# Revit family: VRF_MMYS6HT8P_08-12_Outdoor Unit
name_source: partatom
category: Mechanical Equipment
revit_build: Autodesk Revit 2017 (Build: 20160225_1515(x64)
units: mm (PartAtom-declared; Revit-internal decimal feet)

## family parameters
Always vertical = Yes
Cut with Voids When Loaded = No
OmniClass Number = 23.75.00.00
OmniClass Title = Climate Control (HVAC)
Part Type = Normal
Room Calculation Point = No
Round Connector Dimension = Use Diameter
Shared = No
Work Plane-Based = No

## types (3) — shared parameters
Article Description = SMMSe stand alone
Capacity = -
Compressor detail - Type = Hermetic twin rotary compressor
Content Supplier URL = www.hcltech.com
Depth (mm) = 790 mm  [stored 2.59186 ft]
Description = SMMSe stand alone
Duct diameters(mm) = -
EMCS = 4
ETIM Article Class = EC001213
Energy class = -
Frequency (Hz) = 3Phase , 50Hz
Height (mm) = 1830 mm  [stored 6.00394 ft]
MEPcontent Class = HEATPUMP
Manufacturer = Toshiba
Manufacturer URL = https://www.toshiba-carrier.co.jp
Operating range - Cooling (°C) = -10  -  46
Operating range - Heating (°C) = -25  -  15.5
Part load = 30-100%
Piping diameter(mm)-Gas = 19.1
Piping diameter(mm)-Liquid = 12.7
Product Line = TCTC
Rated efficiency = -
Red = Colour RGB-255 000 000
Refrigerrant Type = R410A
Revit Version = 2017
Starting current = Soft Start
Static pressure = -
URL = https://www.toshiba-carrier.co.jp
Water pipe = -
Weight (Kg) = 227
White = Colour RGB-255 255 255
Width (mm) = 990 mm  [stored 3.24803 ft]

## per-type parameters (varying)
| type | Airflow (m3/h) | Capacities-Cooling (kW) | Capacities-Heating (kW) | Compressor detail - Motor output ( kW) | MCA (A) | MOCP (A) | Power consumption - Cooling | Power consumption - Heating | Rated efficiency - EER / COP | Running current - Cooling | Running current - Heating | Sound pressure - Cooling (dB)(A) | Sound pressure - Heating (dB)(A) | Voltage (V) |
| MMY-SAP0806HT8P-E | 9700 | 22.4 | 25.0 | 2.1 x 2 | 20.5 | 25.0 | 5.54 | 5.65 | 4.04 / 4.42 | 8.79 | 8.96 | 55.0 | 56.0 | 380 - 415V |
| MMY-SAP1006HT8P-E | 9700 | 28.0 | 31.5 | 3.1 x 2 | 21.5 | 25.0 | 7.9 | 7.59 | 3.54 / 4.15 | 12.4 | 11.9 | 57.0 | 58.0 | 380 - 415V |
| MMY-SAP1206HT8P-E | 12,200 | 33.5 | 37.5 | 3.9 x 2 | 26.1 | 32.0 | 10.3 | 9.76 | 3.25 / 3.84 | 16 | 15.1 | 59 | 61 | 380-415V |

note: column(s) folded — value = type name in every type: Article Type, Manufacturer Art. No., Model

note: [stored X ft] marks values corroborated as IEEE doubles in the binary element streams (Revit-internal decimal feet)

## geometry (parser evidence)
native form markers: Sweep x6
no freeform markers — native parametric forms only
